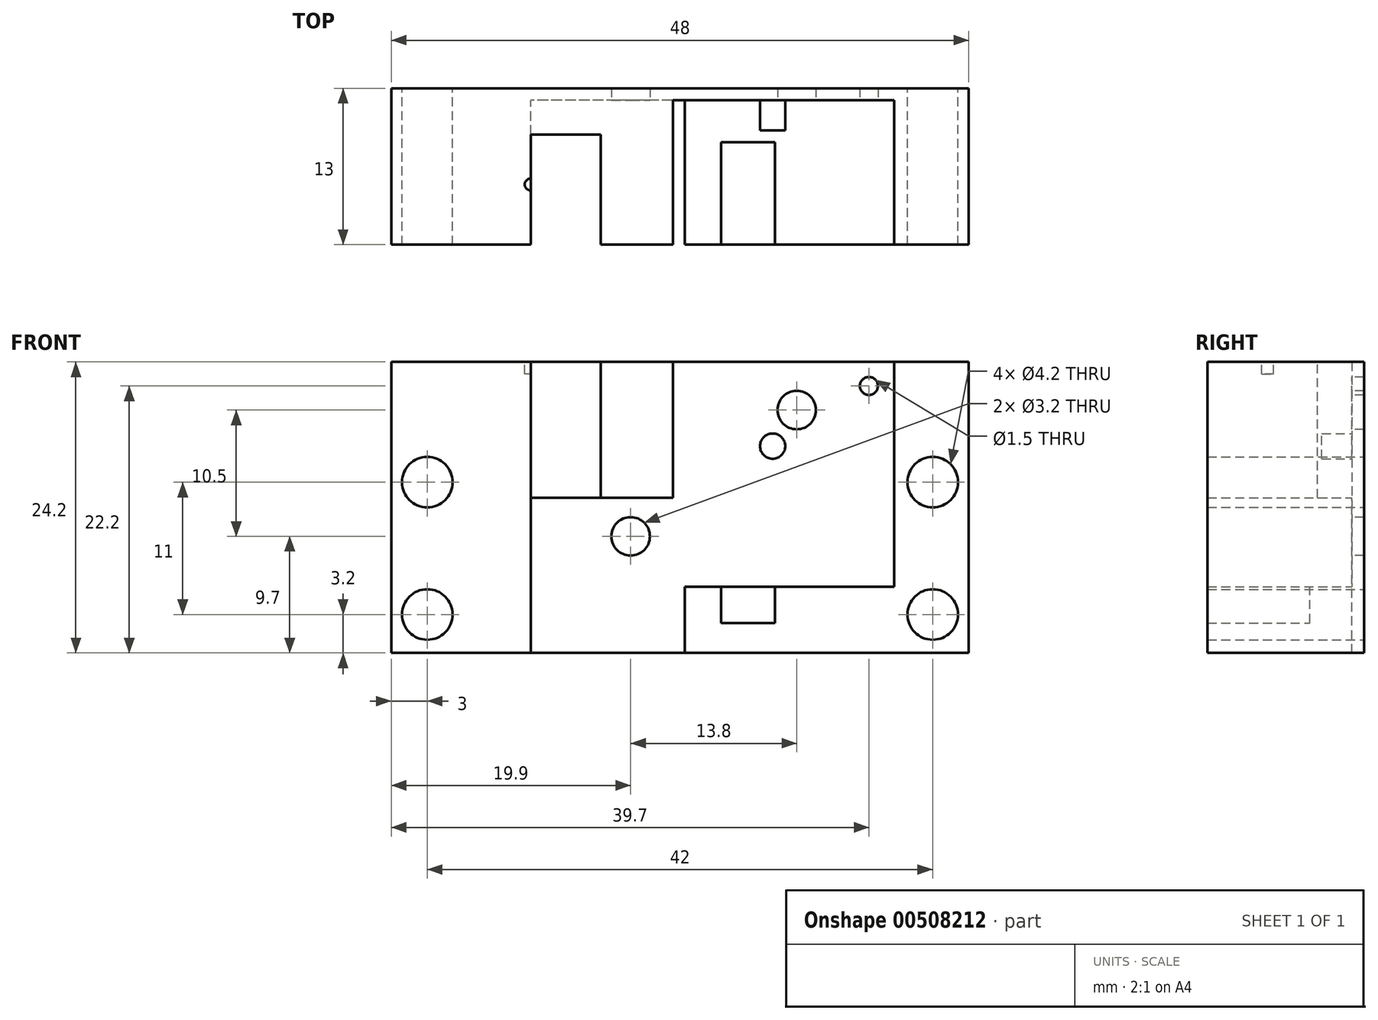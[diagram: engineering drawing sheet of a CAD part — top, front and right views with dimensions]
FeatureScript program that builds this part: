
annotation { "Feature Type Name" : "Feature", "Feature Type Description" : "" }
export const myFeature = defineFeature(function(context is Context, id is Id, definition is map)
    precondition{}
    {
        {
            var Q0;
            Q0=qCreatedBy(makeId("Front.planeOp"),FACE);
            var sketch = newSketch(context, id + "F0", { "sketchPlane" : qUnion([Q0])});
            skLineSegment(sketch, "E0.bottom", {"start": v(24, -12.1) * mm, "end": v(-24, -12.1) * mm});
            skLineSegment(sketch, "E0.top", {"start": v(24, 12.1) * mm, "end": v(-24, 12.1) * mm});
            skLineSegment(sketch, "E0.left", {"start": v(24, -12.1) * mm, "end": v(24, 12.1) * mm});
            skLineSegment(sketch, "E0.right", {"start": v(-24, -12.1) * mm, "end": v(-24, 12.1) * mm});
            skPoint(sketch, "E0.middle", {"position": v(0, 0) * mm});
            skCircle(sketch, "E1", {"center": v(9.7, 8.1) * mm, "radius": 1.6 * mm});
            skCircle(sketch, "E2", {"center": v(-4.1, -2.4) * mm, "radius": 1.6 * mm});
            skSolve(sketch);
        }
        {
            var Q0;
            {var subQ0=sQuery(id+"F0.wireOp",EDGE,"E0.right");Q0=makeQuery(id+"F0.imprint","IMPRINT",FACE,{"disambiguationData":[TD([[makeQuery(id+"F0.imprint","IMPRINT",EDGE,{"derivedFrom":subQ0}),-1.0]])]});}
            var Q1;
            Q1=makeQuery(id+"F0.imprint","IMPRINT",FACE,{"disambiguationData":[TD([[makeQuery(id+"F0.imprint","IMPRINT",EDGE,{"derivedFrom":sQuery(id+"F0.wireOp",EDGE,"E1")}),-1.0]])]});
            var Q2;
            {var subQ4=sQuery(id+"F0.wireOp",EDGE,"E0.left");Q2=makeQuery(id+"F0.imprint","IMPRINT",FACE,{"disambiguationData":[TD([[makeQuery(id+"F0.imprint","IMPRINT",EDGE,{"derivedFrom":subQ4}),1.0]])]});}
            extrude(context, id + "F1", {"entities" : qUnion([Q0, Q1, Q2]), "oppositeDirection" : true, "depth" : 1 * mm, "offsetDistance" : 25 * mm});
        }
        {
            var Q0;
            Q0=makeQuery(id+"F1.opExtrude","CAP_FACE",FACE,{"disambiguationData":[OSD([sQuery(id+"F0.wireOp",EDGE,"E0.bottom"),sQuery(id+"F0.wireOp",EDGE,"E0.top"),sQuery(id+"F0.wireOp",EDGE,"E0.left"),sQuery(id+"F0.wireOp",EDGE,"E0.right"),sQuery(id+"F0.wireOp",EDGE,"E1"),sQuery(id+"F0.wireOp",EDGE,"E2"),sQuery(id+"F0.wireOp",EDGE,"masoxanN-hD2c-xeoc-2SMM-YdOjzVfdmSgA")])],"isStart":true});
            var sketch = newSketch(context, id + "F2", { "sketchPlane" : qUnion([Q0])});
            skLineSegment(sketch, "E3", {"start": v(0.4, -6.6) * mm, "end": v(3.4, -6.6) * mm});
            skLineSegment(sketch, "E4", {"start": v(3.4, -6.6) * mm, "end": v(3.4, -9.6) * mm});
            skLineSegment(sketch, "E5", {"start": v(3.4, -9.6) * mm, "end": v(7.9, -9.6) * mm});
            skLineSegment(sketch, "E6", {"start": v(7.9, -9.6) * mm, "end": v(7.9, -6.6) * mm});
            skLineSegment(sketch, "E7", {"start": v(7.9, -6.6) * mm, "end": v(17.8, -6.6) * mm});
            skLineSegment(sketch, "E8", {"start": v(17.8, -6.6) * mm, "end": v(17.8, -12.1) * mm});
            skLineSegment(sketch, "E9", {"start": v(17.8, -12.1) * mm, "end": v(0.4, -12.1) * mm});
            skLineSegment(sketch, "E10", {"start": v(0.4, -12.1) * mm, "end": v(0.4, -6.6) * mm});
            skCircle(sketch, "E11.0", {"center": v(-4.1, -2.4) * mm, "radius": 1.6 * mm});
            skCircle(sketch, "E12.0", {"center": v(9.7, 8.1) * mm, "radius": 1.6 * mm, "construction": true});
            skCircle(sketch, "E13", {"center": v(15.7, 10.1) * mm, "radius": 0.75 * mm});
            skCircle(sketch, "E14", {"center": v(7.7, 5.1) * mm, "radius": 1.05 * mm});
            skLineSegment(sketch, "E15", {"start": v(3.4, -6.6) * mm, "end": v(7.9, -6.6) * mm});
            skPoint(sketch, "E16.endSnap0", {"position": v(0.4, -9.35) * mm});
            skLineSegment(sketch, "E17.right", {"start": v(-24, 12.1) * mm, "end": v(-24, -12.1) * mm});
            skLineSegment(sketch, "E18.bottom", {"start": v(24, 12.1) * mm, "end": v(17.8, 12.1) * mm});
            skLineSegment(sketch, "E18.top", {"start": v(24, -12.1) * mm, "end": v(17.8, -12.1) * mm});
            skLineSegment(sketch, "E18.left", {"start": v(24, 12.1) * mm, "end": v(24, -12.1) * mm});
            skLineSegment(sketch, "E18.right", {"start": v(17.8, 12.1) * mm, "end": v(17.8, -12.1) * mm});
            skCircle(sketch, "E19", {"center": v(-21, 2.1) * mm, "radius": 2.1 * mm});
            skCircle(sketch, "E20", {"center": v(-21, -8.9) * mm, "radius": 2.1 * mm});
            skCircle(sketch, "E21", {"center": v(21, 2.1) * mm, "radius": 2.1 * mm});
            skCircle(sketch, "E22", {"center": v(21, -8.9) * mm, "radius": 2.1 * mm});
            skLineSegment(sketch, "E23", {"start": v(-0.6, 12.1) * mm, "end": v(-0.6, 0.8) * mm});
            skLineSegment(sketch, "E24", {"start": v(-0.6, 0.8) * mm, "end": v(-6.6, 0.8) * mm});
            skLineSegment(sketch, "E25", {"start": v(-6.6, 0.8) * mm, "end": v(-6.6, 12.1) * mm});
            skLineSegment(sketch, "E26", {"start": v(-12.4, -12.1) * mm, "end": v(-12.4, 12.1) * mm});
            skLineSegment(sketch, "E27", {"start": v(-24, 12.1) * mm, "end": v(-12.4, 12.1) * mm});
            skLineSegment(sketch, "E28", {"start": v(-12.4, 12.1) * mm, "end": v(-0.6, 12.1) * mm});
            skLineSegment(sketch, "E29", {"start": v(-6.6, 0.8) * mm, "end": v(-12.4, 0.8) * mm});
            skSolve(sketch);
        }
        {
            var Q0;
            Q0=makeQuery(id+"F2.imprint","IMPRINT",FACE,{"disambiguationData":[TD([[makeQuery(id+"F2.imprint","IMPRINT",EDGE,{"derivedFrom":sQuery(id+"F2.wireOp",EDGE,"E3")}),-1.0]])]});
            var Q1;
            {var subQ4=sQuery(id+"F2.wireOp",EDGE,"E17.right");Q1=makeQuery(id+"F2.imprint","IMPRINT",FACE,{"disambiguationData":[TD([[makeQuery(id+"F2.imprint","IMPRINT",EDGE,{"derivedFrom":subQ4}),-1.0]])]});}
            var Q2;
            Q2=makeQuery(id+"F2.imprint","IMPRINT",FACE,{"disambiguationData":[TD([[makeQuery(id+"F2.imprint","IMPRINT",EDGE,{"derivedFrom":sQuery(id+"F2.wireOp",EDGE,"E8")}),1.0]])]});
            var Q3;
            {var subQ0=sQuery(id+"F2.wireOp",EDGE,"E23");Q3=makeQuery(id+"F2.imprint","IMPRINT",FACE,{"disambiguationData":[TD([[makeQuery(id+"F2.imprint","IMPRINT",EDGE,{"derivedFrom":subQ0}),-1.0]])]});}
            extrude(context, id + "F3", {"entities" : qUnion([Q0, Q1, Q2, Q3]), "operationType" : NewBodyOperationType.ADD, "depth" : 12 * mm, "offsetDistance" : 25 * mm});
        }
        {
            var Q0;
            Q0=makeQuery(id+"F2.imprint","IMPRINT",FACE,{"disambiguationData":[TD([[makeQuery(id+"F2.imprint","IMPRINT",EDGE,{"derivedFrom":sQuery(id+"F2.wireOp",EDGE,"E4")}),1.0]])]});
            extrude(context, id + "F4", {"entities" : qUnion([Q0]), "operationType" : NewBodyOperationType.ADD, "depth" : 3.5 * mm, "offsetDistance" : 25 * mm});
        }
        {
            var Q0;
            Q0=makeQuery(id+"F2.imprint","IMPRINT",FACE,{"disambiguationData":[TD([[makeQuery(id+"F2.imprint","IMPRINT",EDGE,{"derivedFrom":sQuery(id+"F2.wireOp",EDGE,"E14")}),1.0]])]});
            extrude(context, id + "F5", {"entities" : qUnion([Q0]), "operationType" : NewBodyOperationType.ADD, "depth" : 2.5 * mm, "offsetDistance" : 25 * mm});
        }
        {
            var Q0;
            Q0=makeQuery(id+"F2.imprint","IMPRINT",FACE,{"disambiguationData":[TD([[makeQuery(id+"F2.imprint","IMPRINT",EDGE,{"derivedFrom":sQuery(id+"F2.wireOp",EDGE,"E13")}),1.0]])]});
            extrude(context, id + "F6", {"entities" : qUnion([Q0]), "operationType" : NewBodyOperationType.REMOVE, "endBound" : BoundingType.THROUGH_ALL, "oppositeDirection" : true, "depth" : 25 * mm, "offsetDistance" : 25 * mm});
        }
        {
            var Q0;
            Q0=makeQuery(id+"F2.imprint","IMPRINT",FACE,{"disambiguationData":[TD([[makeQuery(id+"F2.imprint","IMPRINT",EDGE,{"derivedFrom":sQuery(id+"F2.wireOp",EDGE,"E19")}),1.0]])]});
            var Q1;
            Q1=makeQuery(id+"F2.imprint","IMPRINT",FACE,{"disambiguationData":[TD([[makeQuery(id+"F2.imprint","IMPRINT",EDGE,{"derivedFrom":sQuery(id+"F2.wireOp",EDGE,"E21")}),1.0]])]});
            var Q2;
            Q2=makeQuery(id+"F2.imprint","IMPRINT",FACE,{"disambiguationData":[TD([[makeQuery(id+"F2.imprint","IMPRINT",EDGE,{"derivedFrom":sQuery(id+"F2.wireOp",EDGE,"E20")}),1.0]])]});
            var Q3;
            Q3=makeQuery(id+"F2.imprint","IMPRINT",FACE,{"disambiguationData":[TD([[makeQuery(id+"F2.imprint","IMPRINT",EDGE,{"derivedFrom":sQuery(id+"F2.wireOp",EDGE,"E22")}),1.0]])]});
            extrude(context, id + "F7", {"entities" : qUnion([Q0, Q1, Q2, Q3]), "operationType" : NewBodyOperationType.REMOVE, "endBound" : BoundingType.THROUGH_ALL, "depth" : 25 * mm, "offsetDistance" : 25 * mm, "hasSecondDirection" : true, "secondDirectionBound" : BoundingType.THROUGH_ALL, "secondDirectionOppositeDirection" : true, "secondDirectionDepth" : 25 * mm});
        }
        {
            var Q0;
            {var subQ0=sQuery(id+"F2.wireOp",EDGE,"E25");Q0=makeQuery(id+"F2.imprint","IMPRINT",FACE,{"disambiguationData":[TD([[makeQuery(id+"F2.imprint","IMPRINT",EDGE,{"derivedFrom":subQ0}),1.0]])]});}
            extrude(context, id + "F8", {"entities" : qUnion([Q0]), "operationType" : NewBodyOperationType.ADD, "depth" : 2.85 * mm, "offsetDistance" : 25 * mm});
        }
        {
            var Q0;
            {var subQ0=sQuery(id+"F2.wireOp",EDGE,"E28");Q0=makeQuery(id+"F8.boolean.opBoolean","MERGE",FACE,{"derivedFrom":[makeQuery(id+"FKpmHAySgFRZhqA_1.boolean.opBoolean","MERGE",FACE,{"derivedFrom":[makeQuery(id+"F1.opExtrude","SWEPT_FACE",FACE,{"disambiguationData":[OSD([sQuery(id+"F0.wireOp",EDGE,"E0.top")])]}),makeQuery(id+"FKpmHAySgFRZhqA_1.opExtrude","SWEPT_FACE",FACE,{"disambiguationData":[OSD([sQuery(id+"F2.wireOp",EDGE,"E18.bottom")])]}),makeQuery(id+"FKpmHAySgFRZhqA_1.opExtrude","SWEPT_FACE",FACE,{"disambiguationData":[OSD([sQuery(id+"F2.wireOp",EDGE,"E27")])]}),makeQuery(id+"FKpmHAySgFRZhqA_1.opExtrude","SWEPT_FACE",FACE,{"disambiguationData":[OSD([subQ0])]})]}),makeQuery(id+"F8.opExtrude","SWEPT_FACE",FACE,{"disambiguationData":[OSD([subQ0])]})]});}
            var sketch = newSketch(context, id + "F9", { "sketchPlane" : qUnion([Q0])});
            skCircle(sketch, "E30", {"center": v(-12.4, -7) * mm, "radius": 0.5 * mm});
            skSolve(sketch);
        }
        {
            var Q0;
            Q0 = qSketchRegion(id + "F9", true);
            extrude(context, id + "F10", {"entities" : qUnion([Q0]), "operationType" : NewBodyOperationType.REMOVE, "oppositeDirection" : true, "depth" : 1 * mm, "offsetDistance" : 25 * mm});
        }
    });
